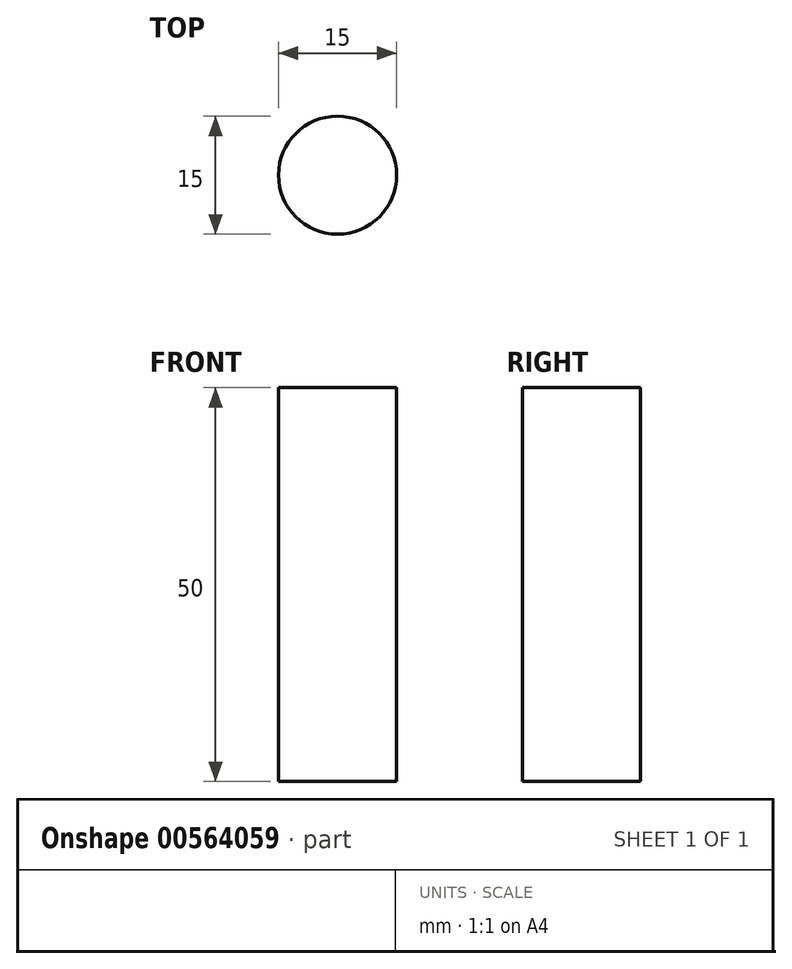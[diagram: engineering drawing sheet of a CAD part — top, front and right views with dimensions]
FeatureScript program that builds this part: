
annotation { "Feature Type Name" : "Feature", "Feature Type Description" : "" }
export const myFeature = defineFeature(function(context is Context, id is Id, definition is map)
    precondition{}
    {
        {
            var Q0;
            Q0=qCreatedBy(makeId("Top.planeOp"),FACE);
            var sketch = newSketch(context, id + "F0", { "sketchPlane" : qUnion([Q0])});
            skCircle(sketch, "E0", {"center": v(0, 0) * mm, "radius": 7.5 * mm});
            skSolve(sketch);
        }
        {
            var Q0;
            Q0=makeQuery(id+"F0.imprint","IMPRINT",FACE,{"disambiguationData":[TD([[makeQuery(id+"F0.imprint","IMPRINT",EDGE,{"derivedFrom":sQuery(id+"F0.wireOp",EDGE,"E0")}),1.0]])]});
            extrude(context, id + "F1", {"entities" : qUnion([Q0]), "depth" : 50 * mm, "offsetDistance" : 25 * mm});
        }
    });
